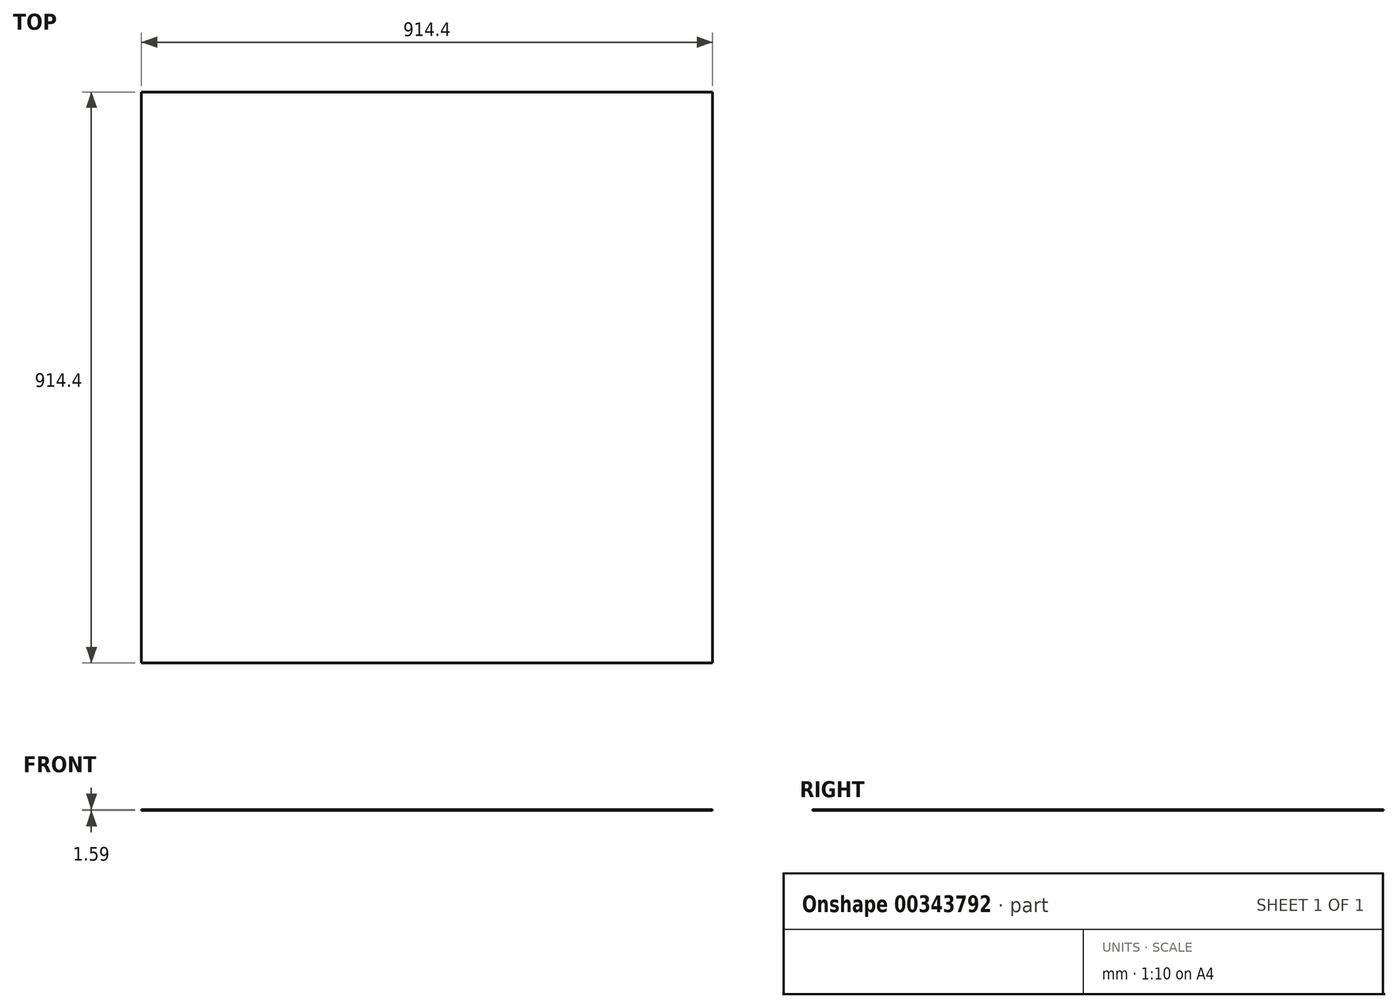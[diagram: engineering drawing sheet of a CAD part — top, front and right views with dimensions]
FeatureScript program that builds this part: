
annotation { "Feature Type Name" : "Feature", "Feature Type Description" : "" }
export const myFeature = defineFeature(function(context is Context, id is Id, definition is map)
    precondition{}
    {
        {
            var Q0;
            Q0=qCreatedBy(makeId("Top.planeOp"),FACE);
            var sketch = newSketch(context, id + "F0", { "sketchPlane" : qUnion([Q0])});
            skLineSegment(sketch, "E0.bottom", {"start": v(457.2, -457.2) * mm, "end": v(-457.2, -457.2) * mm});
            skLineSegment(sketch, "E0.top", {"start": v(457.2, 457.2) * mm, "end": v(-457.2, 457.2) * mm});
            skLineSegment(sketch, "E0.left", {"start": v(457.2, -457.2) * mm, "end": v(457.2, 457.2) * mm});
            skLineSegment(sketch, "E0.right", {"start": v(-457.2, -457.2) * mm, "end": v(-457.2, 457.2) * mm});
            skPoint(sketch, "E0.middle", {"position": v(0, 0) * mm});
            skSolve(sketch);
        }
        {
            var Q0;
            Q0=makeQuery(id+"F0.imprint","IMPRINT",FACE,{"disambiguationData":[TD([[makeQuery(id+"F0.imprint","IMPRINT",EDGE,{"derivedFrom":sQuery(id+"F0.wireOp",EDGE,"E0.bottom")}),-1.0]])]});
            extrude(context, id + "F1", {"entities" : qUnion([Q0]), "depth" : 1.59 * mm});
        }
    });
